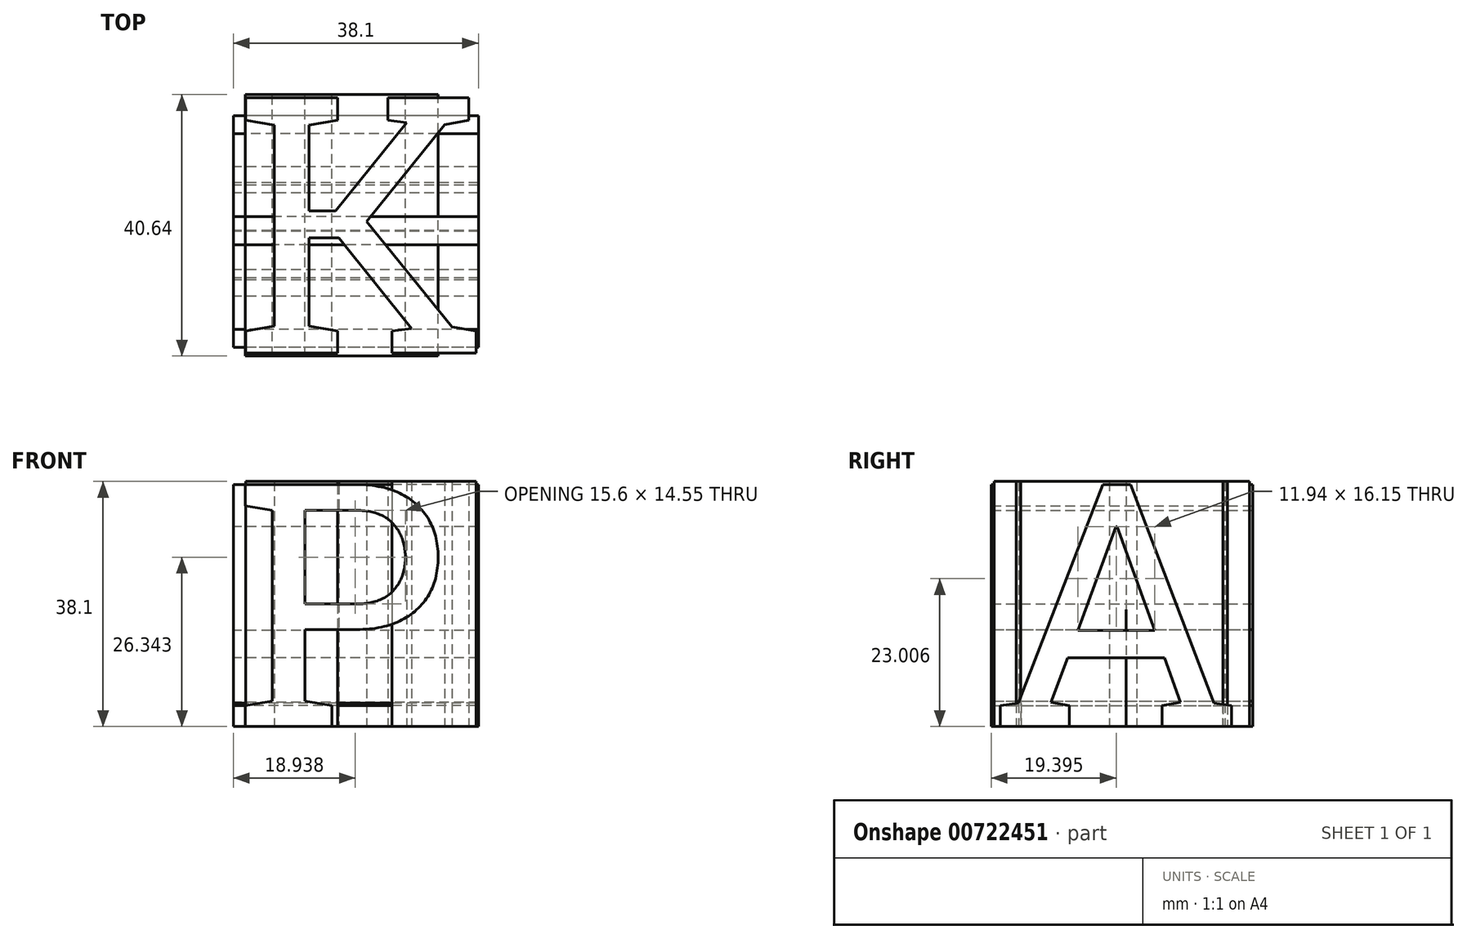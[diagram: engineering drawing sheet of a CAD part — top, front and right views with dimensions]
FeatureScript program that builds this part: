
annotation { "Feature Type Name" : "Feature", "Feature Type Description" : "" }
export const myFeature = defineFeature(function(context is Context, id is Id, definition is map)
    precondition{}
    {
        {
            var Q0;
            Q0=qCreatedBy(makeId("Front.planeOp"),FACE);
            var sketch = newSketch(context, id + "F0", { "sketchPlane" : qUnion([Q0])});
            skText(sketch, "E0", { "text": "P", "fontName": "RobotoSlab-Regular.ttf"});
            const initialGuessF0  = {"E0": [0, 0, 1, 0, 0.0381]};
            skSetInitialGuess(sketch, initialGuessF0);
            skSolve(sketch);
        }
        {
            var Q0;
            Q0=qCreatedBy(makeId("Right.planeOp"),FACE);
            var sketch = newSketch(context, id + "F1", { "sketchPlane" : qUnion([Q0])});
            skText(sketch, "E1", { "text": "A", "fontName": "RobotoSlab-Regular.ttf"});
            const initialGuessF1  = {"E1": [-0.0407, 0, 1, 0, 0.0381]};
            skSetInitialGuess(sketch, initialGuessF1);
            skSolve(sketch);
        }
        {
            var Q0;
            Q0=qCreatedBy(makeId("Top.planeOp"),FACE);
            var sketch = newSketch(context, id + "F2", { "sketchPlane" : qUnion([Q0])});
            skText(sketch, "E2", { "text": "K", "fontName": "RobotoSlab-Regular.ttf"});
            const initialGuessF2  = {"E2": [0, -0.0402, 1, 0, 0.0402]};
            skSetInitialGuess(sketch, initialGuessF2);
            skSolve(sketch);
        }
        {
            var Q0;
            Q0 = qSketchRegion(id + "F2", true);
            extrude(context, id + "F3", {"entities" : qUnion([Q0]), "depth" : 38.1 * mm, "offsetDistance" : 25.4 * mm});
        }
        {
            var Q0;
            Q0 = qSketchRegion(id + "F0", true);
            extrude(context, id + "F4", {"entities" : qUnion([Q0]), "depth" : 40.64 * mm, "offsetDistance" : 25.4 * mm});
        }
        {
            var Q0;
            Q0 = qSketchRegion(id + "F1", true);
            extrude(context, id + "F5", {"entities" : qUnion([Q0]), "depth" : 38.1 * mm, "offsetDistance" : 25.4 * mm});
        }
    });
